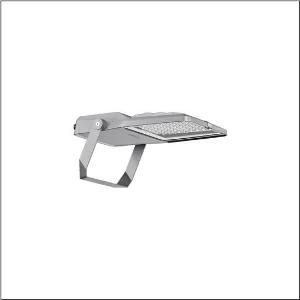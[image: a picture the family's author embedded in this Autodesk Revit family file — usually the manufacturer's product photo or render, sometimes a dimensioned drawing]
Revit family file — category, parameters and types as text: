
# Revit family: floodlight_fl_21_mini___pl43_5xa7776d2a1a_71d0
name_source: partatom
category: Lighting Fixtures
units: mm (PartAtom-declared; Revit-internal decimal feet)

## family parameters
Cut with Voids When Loaded = No
Host = Face
Light Source = No
Part Type = Normal
Room Calculation Point = No
Round Connector Dimension = Use Diameter
Shared = No

## types (1)
- --- (1 x LED, 18300 lm, 142.9 W, 3000K)
    Apparent Load = 143 VA
    CIE Flux Codes = 27 78 99 100 100
    Color Rendering = 70
    Color Temperature = 3000K
    Default Elevation = 1800 mm
    Description = Floodlight FL 21 mini, floodlight, primary light control with lens, of PMMA, primary optical cover: protective disc, of toughened safety glass, transparent, light distribution: PL43, light emission: direct distribution, installation type: surface-mounted, LED, High Power LED, rated luminous flux: 18.300lm, luminous efficacy: 128lm/W, light colour: 730, colour temperature: 3000K, control: flexible luminous flux parameterisation, time-dependent luminous flux control, constant luminous flux control, overheat protection, presetting dimming logarithmic, with terminal, 6-pole, mains connection: 220..240V, AC, 50/60Hz, start of lifetime: 143W, end of service life: 151W, reduction: 63W, luminaire housing, of diecast aluminium, powder-coated, Siteco® metallic grey (DB 702S), corrosivity category C5 mid according to DIN EN ISO 12944, sealing non-destructively replaceable, mounting bracket, of steel, galvanised, powder-coated, Siteco® metallic grey (DB 702S), Smart Interface below and above, protection rating (complete): IP66, insulation class (complete): insulation class II (safety insulation), certification: CE, ENEC, VDE, protection symbol: D, impact resistance: IK08, permissible operating ambient temperature: -40..+40°C, permissible operating ambient temperature for outdoor applications: -40..+50°C, standard: DIN EN 12944, LABS conformity tested according to VDMA 24364:2018-05, packaging unit: 1 piece

Light Distribution: PL43
    Height = 70 mm
    Lamp = 1 x LED
    Lamp Light Flux = 18300 lm
    Lamp Power = 142.9 W
    Lamp count = 1
    Length = 485 mm
    Luminous efficacy = 128 lm/W
    Manufacturer = Siteco
    ModVariant = No
    Model = 5XA7776D2A1A
    Number of Poles = 1
    OnlyDefault = Yes
    Power Factor = 1
    Product Name = Floodlight FL 21 mini | PL43
    Product group = floodlight | pylon annexe
    ProductGroupID = 6200
    Protection Class = Protection class II
    Protection Degree = IP 66
    RLX_Detail_Level = 1
    RLX_Emergency_Light_Flux = 0 lm
    RLX_Emergency_Type = 0
    RLX_Emergency_Type_DB = No
    RlxData = <blob elided: 96049 chars, md5=b8b2bcb7>
    Socket = socket
    Standby Power = 0 W
    System Light Flux = 18300 lm
    System Power = 143 W
    Type Comments = factory setting: luminous flux: 100 % | dim-lin: 254 | 730 mA
    Type Image = l_1006845.jpg
    URL = http://relux.com
    VarID = @adj_093323
    Voltage = 0 V
    Weight = 0.00 kg
    Width = 337 mm

## geometry (parser evidence)
native form markers: Blend x4, Sweep x12
no freeform markers — native parametric forms only
